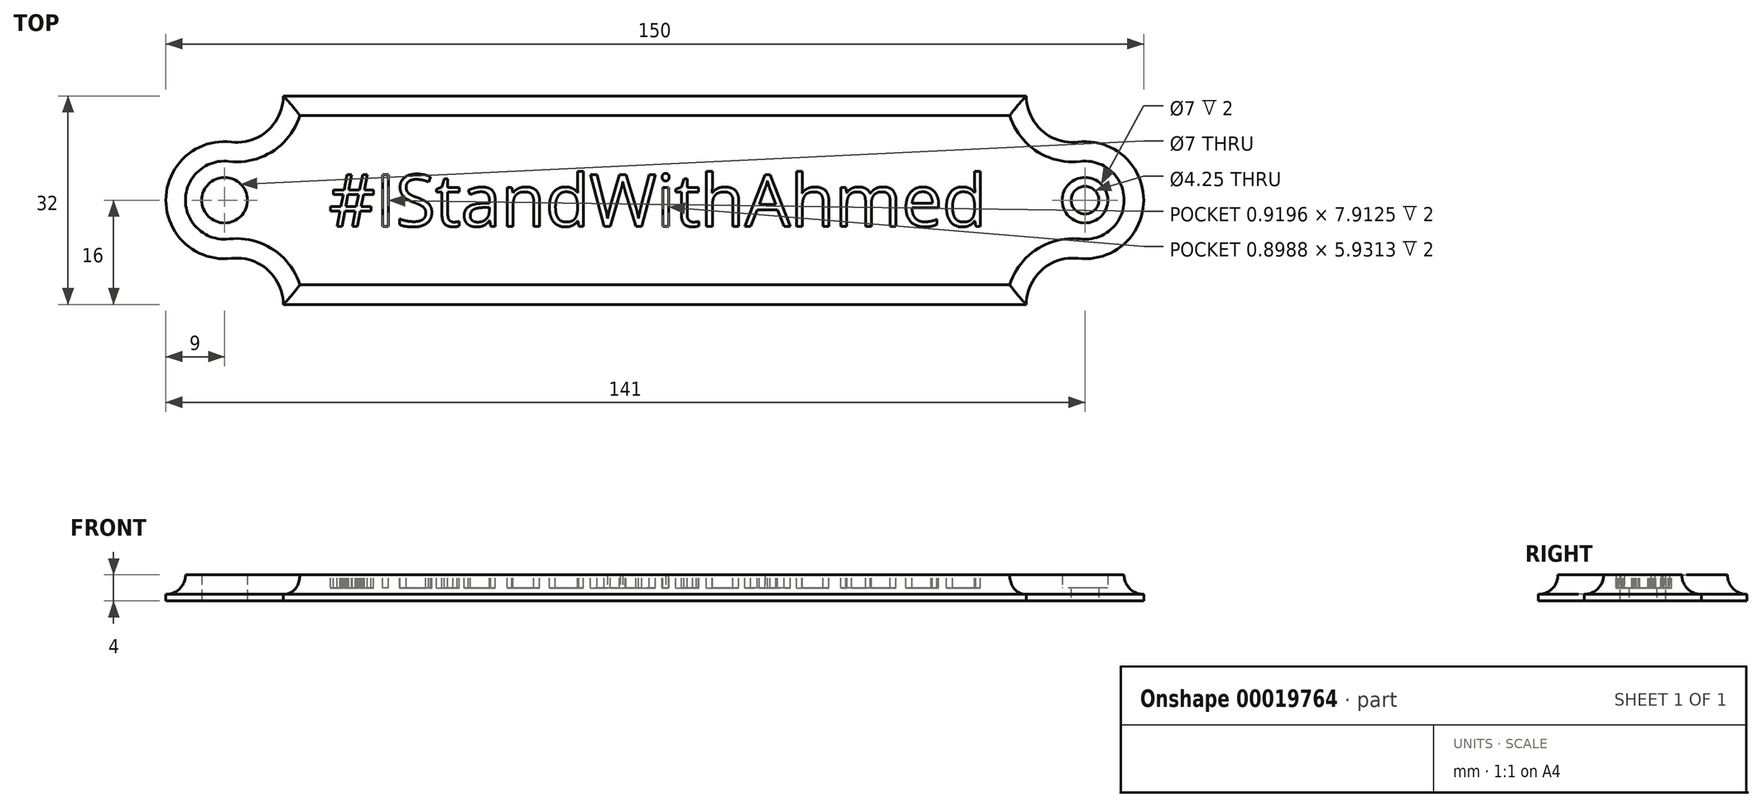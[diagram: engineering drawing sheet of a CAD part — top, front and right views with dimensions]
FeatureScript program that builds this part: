
annotation { "Feature Type Name" : "Feature", "Feature Type Description" : "" }
export const myFeature = defineFeature(function(context is Context, id is Id, definition is map)
    precondition{}
    {
        {
            var Q0;
            Q0=qCreatedBy(makeId("Top.planeOp"),FACE);
            var sketch = newSketch(context, id + "F0", { "sketchPlane" : qUnion([Q0])});
            skLineSegment(sketch, "E0.rect.bottom", {"start": v(57, -16) * mm, "end": v(-57, -16) * mm});
            skLineSegment(sketch, "E0.rect.top", {"start": v(57, 16) * mm, "end": v(-57, 16) * mm});
            skLineSegment(sketch, "E0.rect.left", {"start": v(57, -16) * mm, "end": v(57, 16) * mm});
            skLineSegment(sketch, "E0.rect.right", {"start": v(-57, -16) * mm, "end": v(-57, 16) * mm});
            skPoint(sketch, "E0.rect.middle", {"position": v(0, 0) * mm});
            skCircle(sketch, "E1", {"center": v(66, 0) * mm, "radius": 9 * mm});
            skArc(sketch, "E2", {"start": v(57, 16) * mm, "mid": v(59.39, 10.69) * mm, "end": v(64.94, 8.94) * mm});
            skPoint(sketch, "E2.second.point", {"position": v(71.22, 16) * mm});
            skPoint(sketch, "E2.third.point", {"position": v(64.94, 8.94) * mm});
            skLineSegment(sketch, "E3", {"start": v(0, 0) * mm, "end": v(57, 0) * mm, "construction": true});
            skLineSegment(sketch, "E4", {"start": v(57, 0) * mm, "end": v(0, 0) * mm, "construction": true});
            skLineSegment(sketch, "E5", {"start": v(0, 16) * mm, "end": v(0, 0) * mm, "construction": true});
            skArc(sketch, "E6.MirrorCS", {"start": v(57, -16) * mm, "mid": v(59.39, -10.69) * mm, "end": v(64.94, -8.94) * mm});
            skArc(sketch, "E7.MirrorCS", {"start": v(-57, 16) * mm, "mid": v(-59.39, 10.69) * mm, "end": v(-64.94, 8.94) * mm});
            skCircle(sketch, "E8.MirrorC", {"center": v(-66, 0) * mm, "radius": 9 * mm});
            skArc(sketch, "E9.MirrorCS", {"start": v(-57, -16) * mm, "mid": v(-59.39, -10.69) * mm, "end": v(-64.94, -8.94) * mm});
            skCircle(sketch, "E10", {"center": v(66, 0) * mm, "radius": 2.12 * mm});
            skCircle(sketch, "E11", {"center": v(66, 0) * mm, "radius": 3.5 * mm});
            skCircle(sketch, "E12.MirrorC", {"center": v(-66, 0) * mm, "radius": 3.5 * mm});
            skCircle(sketch, "E13.MirrorC", {"center": v(-66, 0) * mm, "radius": 2.12 * mm});
            skSolve(sketch);
        }
        {
            var Q0;
            Q0 = qSketchRegion(id + "F0", true);
            extrude(context, id + "F1", {"entities" : qUnion([Q0]), "depth" : 4 * mm});
        }
        {
            var Q0;
            Q0=makeQuery(id+"F0.imprint","IMPRINT",FACE,{"disambiguationData":[TD([[makeQuery(id+"F0.imprint","IMPRINT",EDGE,{"derivedFrom":sQuery(id+"F0.wireOp",EDGE,"E12.MirrorC")}),-1.0]])]});
            var Q1;
            Q1=makeQuery(id+"F0.imprint","IMPRINT",FACE,{"disambiguationData":[TD([[makeQuery(id+"F0.imprint","IMPRINT",EDGE,{"derivedFrom":sQuery(id+"F0.wireOp",EDGE,"E10")}),-1.0]])]});
            extrude(context, id + "F2", {"entities" : qUnion([Q0, Q1]), "operationType" : NewBodyOperationType.ADD, "depth" : 2 * mm});
        }
        {
            var Q0;
            Q0=qCreatedBy(makeId("Right.planeOp"),FACE);
            var Q1;
            Q1=makeQuery(id+"F1.opExtrude","CAP_VERTEX",VERTEX,{"disambiguationData":[OSD([sQuery(id+"F0.wireOp",EDGE,"E0.rect.bottom"),sQuery(id+"F0.wireOp",EDGE,"E0.rect.left"),sQuery(id+"F0.wireOp",EDGE,"E6.MirrorCS")])],"isStart":false});
            cPlane(context, id + "F3", {"entities" : qUnion([Q0, Q1]), "cplaneType" : CPlaneType.PLANE_POINT, "offset" : 150 * mm, "width" : 150 * mm, "height" : 150 * mm});
        }
        {
            var Q0;
            Q0=qCreatedBy(id+"F3.planeOp",FACE);
            var sketch = newSketch(context, id + "F4", { "sketchPlane" : qUnion([Q0])});
            skPoint(sketch, "E14.0", {"position": v(-16, 4) * mm});
            skCircle(sketch, "E15", {"center": v(-16, 4) * mm, "radius": 3 * mm});
            skSolve(sketch);
        }
        {
            var Q0;
            Q0=makeQuery(id+"F4.imprint","IMPRINT",FACE,{"disambiguationData":[TD([[makeQuery(id+"F4.imprint","IMPRINT",EDGE,{"derivedFrom":sQuery(id+"F4.wireOp",EDGE,"E15")}),1.0]])]});
            var Q1;
            Q1=makeQuery(id+"F1.opExtrude","CAP_EDGE",EDGE,{"disambiguationData":[OSD([sQuery(id+"F0.wireOp",EDGE,"E0.rect.bottom")])],"isStart":false});
            var Q2;
            Q2=makeQuery(id+"F1.opExtrude","CAP_EDGE",EDGE,{"disambiguationData":[OSD([sQuery(id+"F0.wireOp",EDGE,"E9.MirrorCS")])],"isStart":false});
            var Q3;
            Q3=makeQuery(id+"F1.opExtrude","CAP_EDGE",EDGE,{"disambiguationData":[OSD([sQuery(id+"F0.wireOp",EDGE,"E8.MirrorC")])],"isStart":false});
            var Q4;
            Q4=makeQuery(id+"F1.opExtrude","CAP_EDGE",EDGE,{"disambiguationData":[OSD([sQuery(id+"F0.wireOp",EDGE,"E7.MirrorCS")])],"isStart":false});
            var Q5;
            Q5=makeQuery(id+"F1.opExtrude","CAP_EDGE",EDGE,{"disambiguationData":[OSD([sQuery(id+"F0.wireOp",EDGE,"E0.rect.top")])],"isStart":false});
            var Q6;
            Q6=makeQuery(id+"F1.opExtrude","CAP_EDGE",EDGE,{"disambiguationData":[OSD([sQuery(id+"F0.wireOp",EDGE,"E2")])],"isStart":false});
            var Q7;
            Q7=makeQuery(id+"F1.opExtrude","CAP_EDGE",EDGE,{"disambiguationData":[OSD([sQuery(id+"F0.wireOp",EDGE,"E1")])],"isStart":false});
            var Q8;
            Q8=makeQuery(id+"F1.opExtrude","CAP_EDGE",EDGE,{"disambiguationData":[OSD([sQuery(id+"F0.wireOp",EDGE,"E6.MirrorCS")])],"isStart":false});
            sweep(context, id + "F5", {"operationType" : NewBodyOperationType.REMOVE, "profiles" : qUnion([Q0]), "path" : qUnion([Q1, Q2, Q3, Q4, Q5, Q6, Q7, Q8])});
        }
        {
            var Q0;
            Q0=makeQuery(id+"F1.opExtrude","CAP_FACE",FACE,{"disambiguationData":[OSD([sQuery(id+"F0.wireOp",EDGE,"E0.rect.bottom"),sQuery(id+"F0.wireOp",EDGE,"E0.rect.top"),sQuery(id+"F0.wireOp",EDGE,"E1"),sQuery(id+"F0.wireOp",EDGE,"E2"),sQuery(id+"F0.wireOp",EDGE,"E6.MirrorCS"),sQuery(id+"F0.wireOp",EDGE,"E7.MirrorCS"),sQuery(id+"F0.wireOp",EDGE,"E8.MirrorC"),sQuery(id+"F0.wireOp",EDGE,"E9.MirrorCS"),sQuery(id+"F0.wireOp",EDGE,"E11"),sQuery(id+"F0.wireOp",EDGE,"E12.MirrorC")])],"isStart":false});
            var sketch = newSketch(context, id + "F6", { "sketchPlane" : qUnion([Q0])});
            skText(sketch, "E16", { "text": "#IStandWithAhmed", "fontName": "OpenSans-Regular.ttf"});
            skPoint(sketch, "E17.0", {"position": v(0, 0) * mm});
            const initialGuessF6  = {"E16": [-0.05, -0.004, 1, 0, 0.00798]};
            skSetInitialGuess(sketch, initialGuessF6);
            skSolve(sketch);
        }
        {
            var Q0;
            Q0 = qSketchRegion(id + "F6", true);
            extrude(context, id + "F7", {"entities" : qUnion([Q0]), "operationType" : NewBodyOperationType.REMOVE, "oppositeDirection" : true, "depth" : 2 * mm});
        }
    });
